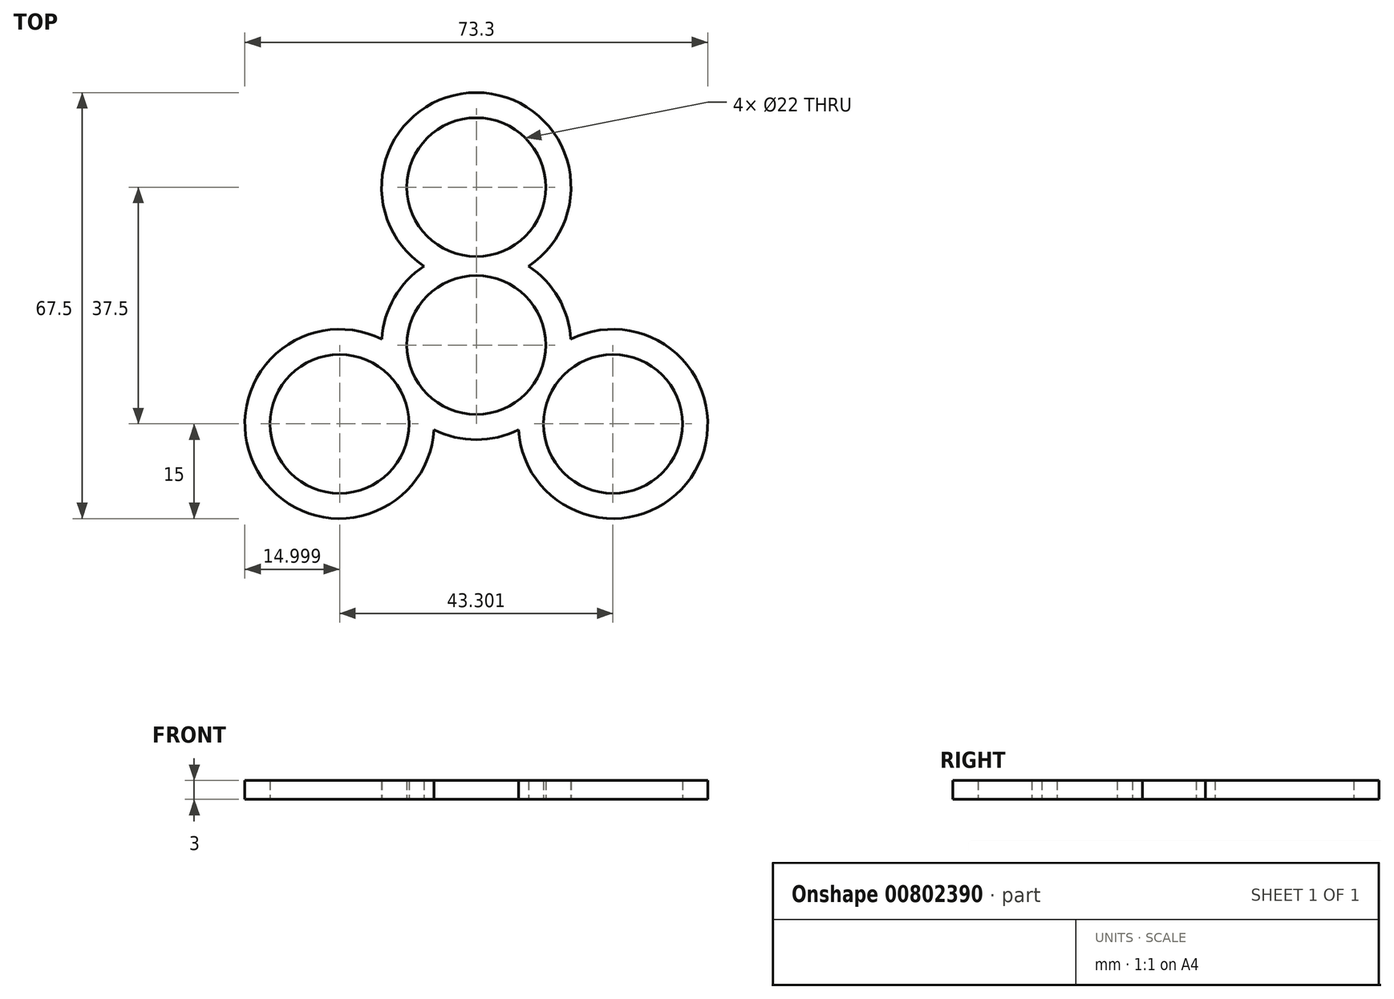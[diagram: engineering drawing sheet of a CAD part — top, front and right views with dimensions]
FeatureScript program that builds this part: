
annotation { "Feature Type Name" : "Feature", "Feature Type Description" : "" }
export const myFeature = defineFeature(function(context is Context, id is Id, definition is map)
    precondition{}
    {
        {
            var Q0;
            Q0=qCreatedBy(makeId("Top.planeOp"),FACE);
            var sketch = newSketch(context, id + "F0", { "sketchPlane" : qUnion([Q0])});
            skArc(sketch, "E0", {"start": v(9.53, 5.5) * mm, "mid": v(0, 11) * mm, "end": v(-9.53, 5.5) * mm});
            skCircle(sketch, "E1", {"center": v(0, 25) * mm, "radius": 11 * mm});
            skArc(sketch, "E2", {"start": v(8.3, 12.5) * mm, "mid": v(0, 40) * mm, "end": v(-8.3, 12.5) * mm});
            skArc(sketch, "E3", {"start": v(-8.3, 12.5) * mm, "mid": v(-10.93, 10.27) * mm, "end": v(-13, 7.5) * mm});
            skArc(sketch, "E4.trimOffspring", {"start": v(13, 7.5) * mm, "mid": v(10.93, 10.27) * mm, "end": v(8.3, 12.5) * mm});
            skArc(sketch, "E5.1.0", {"start": v(-14.97, 0.93) * mm, "mid": v(-34.64, -20) * mm, "end": v(-6.68, -13.43) * mm});
            skCircle(sketch, "E5.1.1", {"center": v(-21.65, -12.5) * mm, "radius": 11 * mm});
            skArc(sketch, "E5.1.2", {"start": v(-9.53, 5.5) * mm, "mid": v(-9.53, -5.5) * mm, "end": v(0, -11) * mm});
            skArc(sketch, "E5.1.3", {"start": v(-6.68, -13.43) * mm, "mid": v(-3.43, -14.6) * mm, "end": v(0, -15) * mm});
            skArc(sketch, "E5.1.4", {"start": v(-13, 7.5) * mm, "mid": v(-14.36, 4.33) * mm, "end": v(-14.97, 0.93) * mm});
            skArc(sketch, "E5.2.0", {"start": v(6.68, -13.43) * mm, "mid": v(34.64, -20) * mm, "end": v(14.97, 0.93) * mm});
            skCircle(sketch, "E5.2.1", {"center": v(21.65, -12.5) * mm, "radius": 11 * mm});
            skArc(sketch, "E5.2.2", {"start": v(0, -11) * mm, "mid": v(9.53, -5.5) * mm, "end": v(9.53, 5.5) * mm});
            skArc(sketch, "E5.2.3", {"start": v(14.97, 0.93) * mm, "mid": v(14.36, 4.33) * mm, "end": v(13, 7.5) * mm});
            skArc(sketch, "E5.2.4", {"start": v(0, -15) * mm, "mid": v(3.43, -14.6) * mm, "end": v(6.68, -13.43) * mm});
            skSolve(sketch);
        }
        {
            var Q0;
            Q0 = qSketchRegion(id + "F0", true);
            extrude(context, id + "F1", {"entities" : qUnion([Q0]), "depth" : 3 * mm, "offsetDistance" : 25 * mm});
        }
    });
